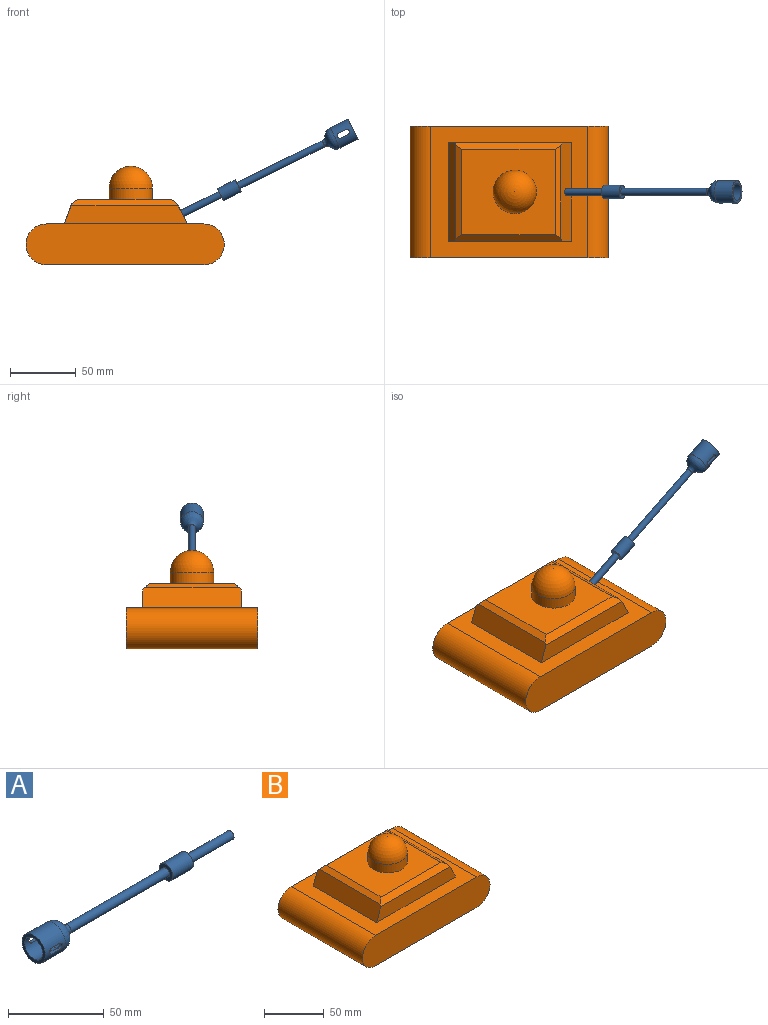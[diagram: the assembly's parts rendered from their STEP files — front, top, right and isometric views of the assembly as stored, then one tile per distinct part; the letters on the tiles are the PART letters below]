
ASSEMBLY  parts=2 mates=1
PART A: 24 faces, bbox 145x17.2x17.2 mm
  f0: cylinder r=6.58mm len=15mm, axis (-1,0,0), area 546.3mm2, adj f2,f15,f16,f17,f18,f19,f20,f21
  f1: cylinder r=8.58mm len=17.17mm, axis (-1,0,0), area 735.2mm2, adj f14,f15,f16,f17,f18,f19,f20,f21
  f2: revolved ~13.17x13.17mm, area 279mm2, adj f0,f3
  f3: cylinder r=0.62mm len=74.53mm, axis (-1,0,0), area 291.4mm2, adj f2,f4
  f4: plane 6.25x6.25mm, normal (1,0,0), area 29.4mm2, adj f3,f5
  f5: cylinder r=3.12mm len=11mm, axis (-1,0,0), area 215.8mm2, adj f4,f6
  f6: plane 6.25x6.25mm, normal (-1,0,0), area 29.4mm2, adj f5,f7
  f7: cylinder r=0.62mm len=34.5mm, axis (-1,0,0), area 134.9mm2, adj f6,f8
  f8: plane 5.24x5.24mm, normal (1,0,0), area 20.4mm2, adj f7,f9
  f9: cylinder r=2.62mm len=32.5mm, axis (-1,0,0), area 535.5mm2, adj f8,f10
  f10: plane 10.25x10.25mm, normal (1,0,0), area 60.8mm2, adj f9,f11
  f11: cylinder r=5.12mm len=15mm, axis (-1,0,0), area 482.8mm2, adj f10,f12
  f12: plane 10.25x10.25mm, normal (-1,0,0), area 60.8mm2, adj f11,f13
  f13: cylinder r=2.62mm len=72.5mm, axis (-1,0,0), area 1194.6mm2, adj f12,f14
  f14: revolved ~17.17x17.17mm, area 459.1mm2, adj f1,f13
  f15: plane 17.17x17.17mm, normal (-1,0,0), area 95.3mm2, adj f0,f1
  f16: cylinder r=2mm len=4mm, axis (0,-1,0), area 12.8mm2, adj f0,f1,f17,f19
  f17: plane 6x2.08mm, normal (0,0,-1), area 12.4mm2, adj f0,f1,f16,f18
  f18: cylinder r=2mm len=4mm, axis (0,-1,0), area 12.8mm2, adj f0,f1,f17,f19
  f19: plane 6x2.08mm, normal (0,0,1), area 12.4mm2, adj f0,f1,f16,f18
  f20: plane 6x2.08mm, normal (0,0,1), area 12.4mm2, adj f0,f1,f21,f23
  f21: cylinder r=2mm len=4mm, axis (0,-1,0), area 12.8mm2, adj f0,f1,f20,f22
  f22: plane 6x2.08mm, normal (0,0,-1), area 12.4mm2, adj f0,f1,f21,f23
  f23: cylinder r=2mm len=4mm, axis (0,-1,0), area 12.8mm2, adj f0,f1,f20,f22
PART B: 17 faces, bbox 150.9x100x75 mm
  f0: cylinder r=15.6mm len=100mm, axis (0,1,0), area 4900.3mm2, adj f1,f3,f4,f5
  f1: plane 119.73x100mm, normal (0,0,1), area 4960.4mm2, adj f0,f2,f4,f5,f6,f7,f9,f10
  f2: cylinder r=15.6mm len=100mm, axis (0,1,0), area 4900.3mm2, adj f1,f3,f4,f5
  f3: plane 119.73x100mm, normal (0,0,-1), area 11972.6mm2, adj f0,f2,f4,f5
  f4: plane 150.92x31.2mm, normal (0,-1,0), area 4499.3mm2, adj f0,f1,f2,f3
  f5: plane 150.92x31.2mm, normal (0,1,0), area 4499.3mm2, adj f0,f1,f2,f3
  f6: plane 75x15.38mm, normal (-0.94,0,0.34), area 1221.6mm2, adj f1,f9,f10,f14,f15,f16
  f7: plane 75x15.91mm, normal (0.9,0,0.44), area 1325.2mm2, adj f1,f9,f10,f13,f14,f15
  f8: plane 70.96x65mm, normal (0,0,1), area 3756.9mm2, adj f11,f13,f14,f15,f16
  f9: plane 93.5x13.7mm, normal (0,-1,0), area 1200.6mm2, adj f1,f6,f7,f14
  f10: plane 93.5x13.7mm, normal (0,1,0), area 1200.6mm2, adj f1,f6,f7,f15
  f11: cylinder r=16.5mm len=33mm, axis (0,0,-1), area 896mm2, adj f8,f12
  f12: sphere r=16.5mm, area 1710.5mm2, adj f11
  f13: plane 70.57x4.48mm, normal (0.53,0,0.85), area 357.8mm2, adj f7,f8,f14,f15
  f14: plane 81.84x5mm, normal (0,-0.71,0.71), area 549.3mm2, adj f6,f7,f8,f9,f13,f16
  f15: plane 81.84x5mm, normal (0,0.71,0.71), area 549.3mm2, adj f6,f7,f8,f10,f13,f16
  f16: plane 71.64x4.71mm, normal (-0.58,0,0.82), area 393.5mm2, adj f6,f8,f14,f15
PLACE A rot(axis=(0,1,0),153.7deg) t=(87.17,-2.33,55.26)mm
PLACE B t=(-10.01,-2.33,5.17)mm
MATE fastened A.f0 <-> B.f7  axis (-0.9,0,-0.44) through (33.37,-2.33,28.69)mm
